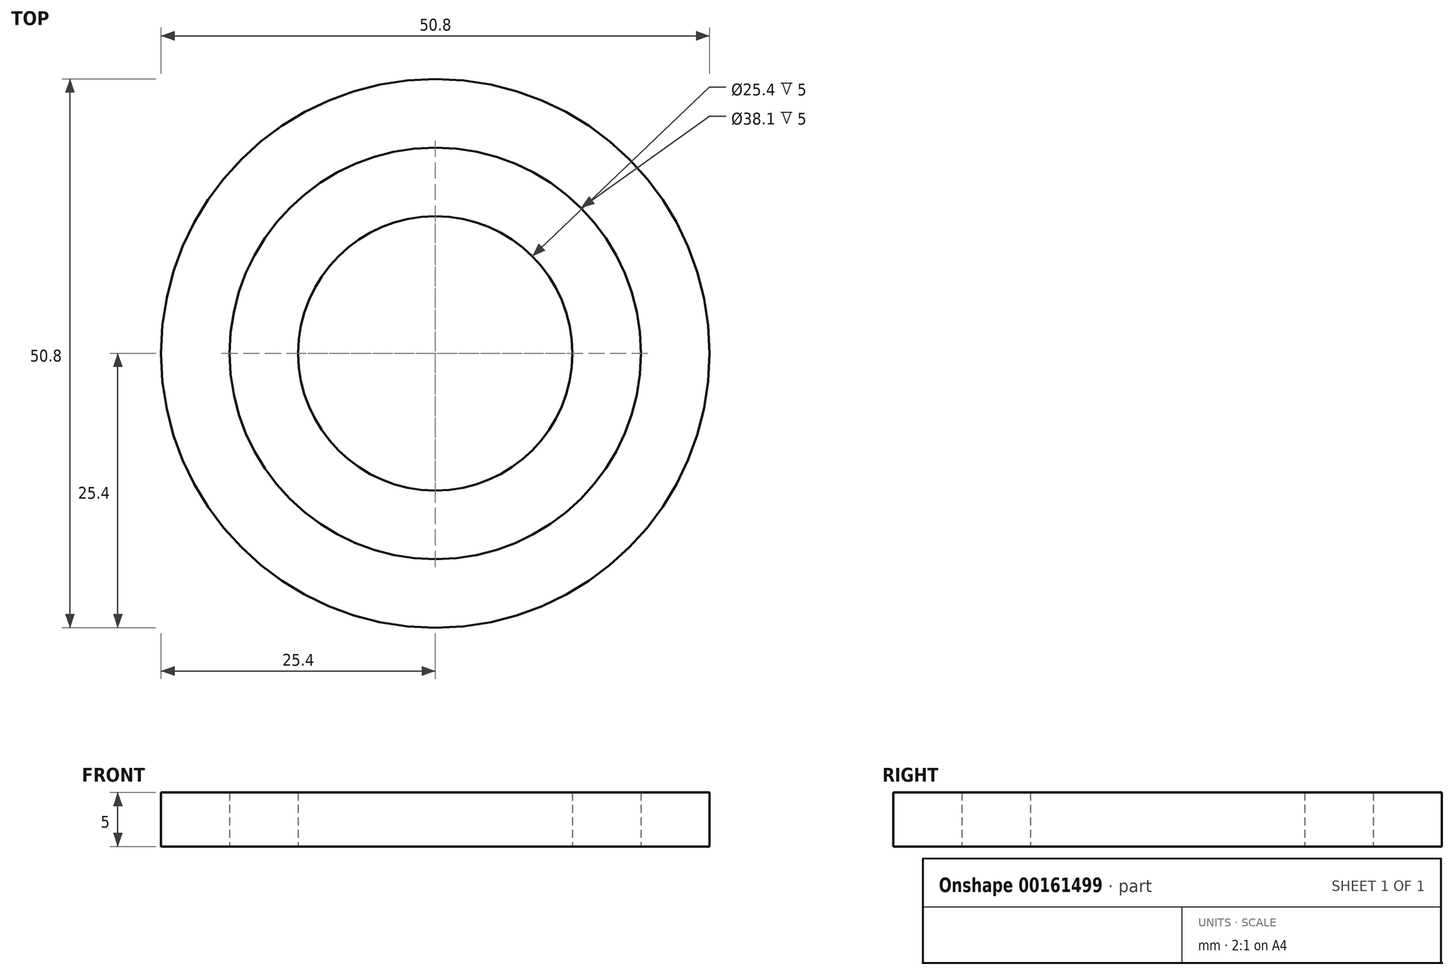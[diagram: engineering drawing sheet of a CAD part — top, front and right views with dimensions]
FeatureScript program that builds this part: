
annotation { "Feature Type Name" : "Feature", "Feature Type Description" : "" }
export const myFeature = defineFeature(function(context is Context, id is Id, definition is map)
    precondition{}
    {
        {
            var Q0;
            Q0=qCreatedBy(makeId("Top.planeOp"),FACE);
            var sketch = newSketch(context, id + "F0", { "sketchPlane" : qUnion([Q0])});
            skCircle(sketch, "E0", {"center": v(0, 0) * mm, "radius": 12.7 * mm});
            skCircle(sketch, "E1", {"center": v(0, 0) * mm, "radius": 19.05 * mm});
            skCircle(sketch, "E2", {"center": v(0, 0) * mm, "radius": 25.4 * mm});
            skSolve(sketch);
        }
        {
            var Q0;
            Q0 = qSketchRegion(id + "F0", true);
            extrude(context, id + "F1", {"entities" : qUnion([Q0]), "depth" : 5 * mm});
        }
        {
            var Q0;
            Q0=makeQuery(id+"F0.imprint","IMPRINT",FACE,{"disambiguationData":[TD([[makeQuery(id+"F0.imprint","IMPRINT",EDGE,{"derivedFrom":sQuery(id+"F0.wireOp",EDGE,"E0")}),-1.0]])]});
            extrude(context, id + "F2", {"entities" : qUnion([Q0]), "depth" : 5 * mm});
        }
    });
